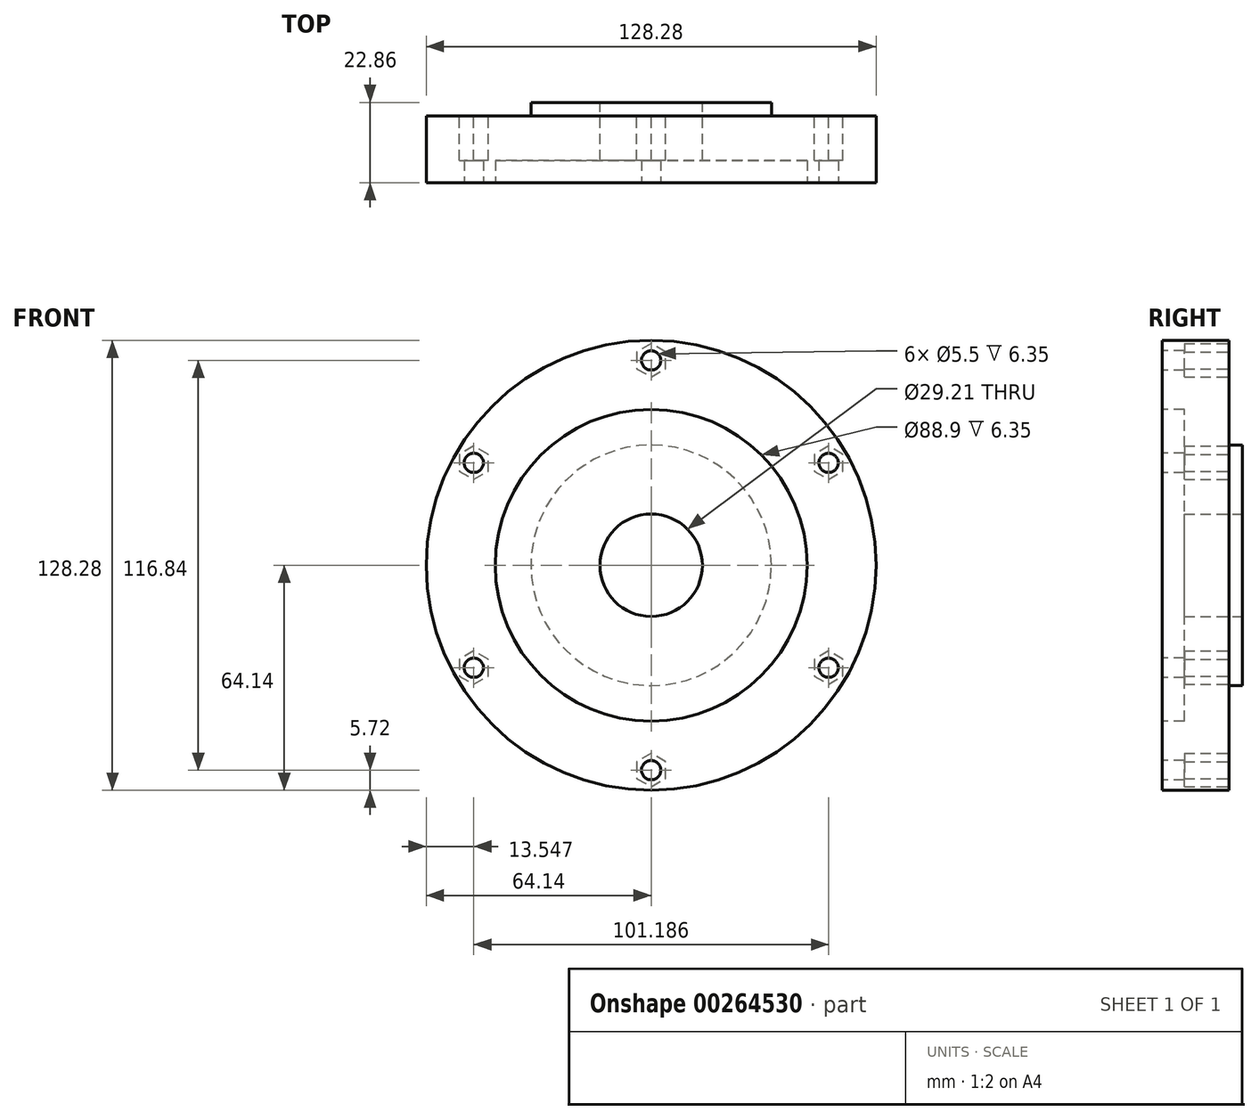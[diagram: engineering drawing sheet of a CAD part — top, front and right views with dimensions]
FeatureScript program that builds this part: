
annotation { "Feature Type Name" : "Feature", "Feature Type Description" : "" }
export const myFeature = defineFeature(function(context is Context, id is Id, definition is map)
    precondition{}
    {
        {
            var Q0;
            Q0=qCreatedBy(makeId("Front.planeOp"),FACE);
            var sketch = newSketch(context, id + "F0", { "sketchPlane" : qUnion([Q0])});
            skCircle(sketch, "E0", {"center": v(0, 0) * mm, "radius": 64.13 * mm});
            skSolve(sketch);
        }
        {
            var Q0;
            Q0 = qSketchRegion(id + "F0", true);
            extrude(context, id + "F1", {"entities" : qUnion([Q0]), "depth" : 19.05 * mm});
        }
        {
            var Q0;
            Q0=makeQuery(id+"F1.opExtrude","CAP_FACE",FACE,{"disambiguationData":[OSD([sQuery(id+"F0.wireOp",EDGE,"E0")])],"isStart":true});
            var sketch = newSketch(context, id + "F2", { "sketchPlane" : qUnion([Q0])});
            skCircle(sketch, "E1", {"center": v(0, 0) * mm, "radius": 14.6 * mm});
            skSolve(sketch);
        }
        {
            var Q0;
            Q0=makeQuery(id+"F1.opExtrude","CAP_FACE",FACE,{"disambiguationData":[OSD([sQuery(id+"F0.wireOp",EDGE,"E0")])],"isStart":true});
            var sketch = newSketch(context, id + "F3", { "sketchPlane" : qUnion([Q0])});
            skCircle(sketch, "E2", {"center": v(0, 0) * mm, "radius": 34.3 * mm});
            skSolve(sketch);
        }
        {
            var Q0;
            Q0 = qSketchRegion(id + "F3", true);
            extrude(context, id + "F4", {"entities" : qUnion([Q0]), "operationType" : NewBodyOperationType.ADD, "depth" : 3.8 * mm});
        }
        {
            var Q0;
            Q0=makeQuery(id+"F1.opExtrude","CAP_FACE",FACE,{"disambiguationData":[OSD([sQuery(id+"F0.wireOp",EDGE,"E0")])],"isStart":false});
            var sketch = newSketch(context, id + "F5", { "sketchPlane" : qUnion([Q0])});
            skCircle(sketch, "E3", {"center": v(0, 0) * mm, "radius": 12.7 * mm});
            skSolve(sketch);
        }
        {
            var Q0;
            Q0 = qSketchRegion(id + "F5", true);
            extrude(context, id + "F6", {"entities" : qUnion([Q0]), "operationType" : NewBodyOperationType.REMOVE, "endBound" : BoundingType.THROUGH_ALL, "oppositeDirection" : true, "depth" : 25.4 * mm});
        }
        {
            var Q0;
            Q0=makeQuery(id+"F1.opExtrude","CAP_FACE",FACE,{"disambiguationData":[OSD([sQuery(id+"F0.wireOp",EDGE,"E0")])],"isStart":false});
            var sketch = newSketch(context, id + "F7", { "sketchPlane" : qUnion([Q0])});
            skCircle(sketch, "E4", {"center": v(0, 0) * mm, "radius": 44.45 * mm});
            skSolve(sketch);
        }
        {
            var Q0;
            Q0 = qSketchRegion(id + "F2", true);
            extrude(context, id + "F8", {"entities" : qUnion([Q0]), "operationType" : NewBodyOperationType.REMOVE, "endBound" : BoundingType.THROUGH_ALL, "oppositeDirection" : true, "depth" : 25.4 * mm, "hasSecondDirection" : true, "secondDirectionBound" : BoundingType.THROUGH_ALL, "secondDirectionOppositeDirection" : false, "secondDirectionDepth" : 25.4 * mm});
        }
        {
            var Q0;
            Q0 = qSketchRegion(id + "F7", true);
            extrude(context, id + "F9", {"entities" : qUnion([Q0]), "operationType" : NewBodyOperationType.REMOVE, "oppositeDirection" : true, "depth" : 6.35 * mm});
        }
        {
            var Q0;
            Q0=makeQuery(id+"F9.boolean.opBoolean","COPY",FACE,{"derivedFrom":makeQuery(id+"F9.opExtrude","CAP_FACE",FACE,{"disambiguationData":[OSD([sQuery(id+"F7.wireOp",EDGE,"E4")])],"isStart":false})});
            var sketch = newSketch(context, id + "F14", { "sketchPlane" : qUnion([Q0])});
            skCircle(sketch, "E5", {"center": v(0, 0) * mm, "radius": 27.94 * mm});
            skSolve(sketch);
        }
        {
            var Q0;
            Q0=makeQuery(id+"F1.opExtrude","CAP_FACE",FACE,{"disambiguationData":[OSD([sQuery(id+"F0.wireOp",EDGE,"E0")])],"isStart":true});
            var sketch = newSketch(context, id + "F10", { "sketchPlane" : qUnion([Q0])});
            skSolve(sketch);
        }
        {
            var Q0;
            Q0=makeQuery(id+"F10.imprint","IMPRINT",FACE,{"disambiguationData":[TD([[makeQuery(id+"F10.imprint","IMPRINT",EDGE,{"derivedFrom":makeQuery(id+"F1.opExtrude","CAP_EDGE",EDGE,{"disambiguationData":[OSD([sQuery(id+"F0.wireOp",EDGE,"E0")])],"isStart":true})}),-1.0]])]});
            var sketch = newSketch(context, id + "F11", { "sketchPlane" : qUnion([Q0])});
            skCircle(sketch, "E6.cCircle", {"center": v(0, 0) * mm, "radius": 58.42 * mm, "construction": true});
            skLineSegment(sketch, "E6.0", {"start": v(50.6, 29.2) * mm, "end": v(50.6, -29.2) * mm, "construction": true});
            skLineSegment(sketch, "E6.1", {"start": v(50.6, -29.2) * mm, "end": v(0, -58.42) * mm, "construction": true});
            skLineSegment(sketch, "E6.2", {"start": v(0, -58.42) * mm, "end": v(-50.6, -29.2) * mm, "construction": true});
            skLineSegment(sketch, "E6.3", {"start": v(-50.6, -29.2) * mm, "end": v(-50.6, 29.2) * mm, "construction": true});
            skLineSegment(sketch, "E6.4", {"start": v(-50.6, 29.2) * mm, "end": v(0, 58.42) * mm, "construction": true});
            skLineSegment(sketch, "E6.5", {"start": v(0, 58.42) * mm, "end": v(50.6, 29.2) * mm, "construction": true});
            skCircle(sketch, "E7.cCircle", {"center": v(0, -58.42) * mm, "radius": 4.75 * mm, "construction": true});
            skLineSegment(sketch, "E7.0", {"start": v(4.11, -56.05) * mm, "end": v(4.11, -60.8) * mm});
            skLineSegment(sketch, "E7.1", {"start": v(4.11, -60.8) * mm, "end": v(0, -63.17) * mm});
            skLineSegment(sketch, "E7.2", {"start": v(0, -63.17) * mm, "end": v(-4.11, -60.8) * mm});
            skLineSegment(sketch, "E7.3", {"start": v(-4.11, -60.8) * mm, "end": v(-4.11, -56.04) * mm});
            skLineSegment(sketch, "E7.4", {"start": v(-4.11, -56.04) * mm, "end": v(0, -53.67) * mm});
            skLineSegment(sketch, "E7.5", {"start": v(0, -53.67) * mm, "end": v(4.11, -56.05) * mm});
            skCircle(sketch, "E8.1.0", {"center": v(50.6, -29.21) * mm, "radius": 4.75 * mm, "construction": true});
            skLineSegment(sketch, "E8.1.1", {"start": v(46.48, -31.58) * mm, "end": v(46.48, -26.83) * mm});
            skLineSegment(sketch, "E8.1.2", {"start": v(54.7, -31.59) * mm, "end": v(50.6, -33.96) * mm});
            skLineSegment(sketch, "E8.1.3", {"start": v(50.6, -33.96) * mm, "end": v(46.48, -31.58) * mm});
            skLineSegment(sketch, "E8.1.4", {"start": v(50.6, -24.46) * mm, "end": v(54.7, -26.84) * mm});
            skLineSegment(sketch, "E8.1.5", {"start": v(54.7, -26.84) * mm, "end": v(54.7, -31.59) * mm});
            skLineSegment(sketch, "E8.1.6", {"start": v(46.48, -26.83) * mm, "end": v(50.6, -24.46) * mm});
            skCircle(sketch, "E8.2.0", {"center": v(50.6, 29.2) * mm, "radius": 4.75 * mm, "construction": true});
            skLineSegment(sketch, "E8.2.1", {"start": v(50.6, 24.46) * mm, "end": v(46.48, 26.83) * mm});
            skLineSegment(sketch, "E8.2.2", {"start": v(54.7, 31.58) * mm, "end": v(54.7, 26.83) * mm});
            skLineSegment(sketch, "E8.2.3", {"start": v(54.7, 26.83) * mm, "end": v(50.6, 24.46) * mm});
            skLineSegment(sketch, "E8.2.4", {"start": v(46.48, 31.58) * mm, "end": v(50.6, 33.96) * mm});
            skLineSegment(sketch, "E8.2.5", {"start": v(50.6, 33.96) * mm, "end": v(54.7, 31.58) * mm});
            skLineSegment(sketch, "E8.2.6", {"start": v(46.48, 26.83) * mm, "end": v(46.48, 31.58) * mm});
            skCircle(sketch, "E8.3.0", {"center": v(0, 58.42) * mm, "radius": 4.75 * mm, "construction": true});
            skLineSegment(sketch, "E8.3.1", {"start": v(4.11, 56.04) * mm, "end": v(0, 53.67) * mm});
            skLineSegment(sketch, "E8.3.2", {"start": v(0, 63.17) * mm, "end": v(4.11, 60.8) * mm});
            skLineSegment(sketch, "E8.3.3", {"start": v(4.11, 60.8) * mm, "end": v(4.11, 56.04) * mm});
            skLineSegment(sketch, "E8.3.4", {"start": v(-4.11, 56.05) * mm, "end": v(-4.11, 60.8) * mm});
            skLineSegment(sketch, "E8.3.5", {"start": v(-4.11, 60.8) * mm, "end": v(0, 63.17) * mm});
            skLineSegment(sketch, "E8.3.6", {"start": v(0, 53.67) * mm, "end": v(-4.11, 56.05) * mm});
            skCircle(sketch, "E8.4.0", {"center": v(-50.6, 29.21) * mm, "radius": 4.75 * mm, "construction": true});
            skLineSegment(sketch, "E8.4.1", {"start": v(-46.48, 31.59) * mm, "end": v(-46.48, 26.83) * mm});
            skLineSegment(sketch, "E8.4.2", {"start": v(-54.7, 31.59) * mm, "end": v(-50.6, 33.96) * mm});
            skLineSegment(sketch, "E8.4.3", {"start": v(-50.6, 33.96) * mm, "end": v(-46.48, 31.58) * mm});
            skLineSegment(sketch, "E8.4.4", {"start": v(-50.6, 24.46) * mm, "end": v(-54.7, 26.84) * mm});
            skLineSegment(sketch, "E8.4.5", {"start": v(-54.7, 26.84) * mm, "end": v(-54.7, 31.59) * mm});
            skLineSegment(sketch, "E8.4.6", {"start": v(-46.48, 26.84) * mm, "end": v(-50.6, 24.46) * mm});
            skCircle(sketch, "E8.5.0", {"center": v(-50.6, -29.2) * mm, "radius": 4.75 * mm, "construction": true});
            skLineSegment(sketch, "E8.5.1", {"start": v(-50.6, -24.46) * mm, "end": v(-46.48, -26.84) * mm});
            skLineSegment(sketch, "E8.5.2", {"start": v(-54.7, -31.58) * mm, "end": v(-54.7, -26.83) * mm});
            skLineSegment(sketch, "E8.5.3", {"start": v(-54.7, -26.83) * mm, "end": v(-50.6, -24.46) * mm});
            skLineSegment(sketch, "E8.5.4", {"start": v(-46.48, -31.58) * mm, "end": v(-50.6, -33.96) * mm});
            skLineSegment(sketch, "E8.5.5", {"start": v(-50.6, -33.96) * mm, "end": v(-54.7, -31.58) * mm});
            skLineSegment(sketch, "E8.5.6", {"start": v(-46.48, -26.84) * mm, "end": v(-46.48, -31.59) * mm});
            skSolve(sketch);
        }
        {
            var Q0;
            Q0 = qSketchRegion(id + "F11", true);
            extrude(context, id + "F12", {"entities" : qUnion([Q0]), "operationType" : NewBodyOperationType.REMOVE, "oppositeDirection" : true, "depth" : 12.7 * mm});
        }
        {
            var Q0;
            Q0=sQuery(id+"F11.wireOp",VERTEX,"E8.2.0.center");
            var Q1;
            Q1=sQuery(id+"F11.wireOp",VERTEX,"E8.1.0.center");
            var Q2;
            Q2=sQuery(id+"F11.wireOp",VERTEX,"E7.cCircle.center");
            var Q3;
            Q3=sQuery(id+"F11.wireOp",VERTEX,"E6.3.start");
            var Q4;
            Q4=sQuery(id+"F11.wireOp",VERTEX,"E6.4.start");
            var Q5;
            Q5=sQuery(id+"F11.wireOp",VERTEX,"E6.5.start");
            var Q6;
            Q6=makeQuery(id+"F1.opExtrude","SWEPT_BODY",BODY,{"disambiguationData":[OSD([sQuery(id+"F0.wireOp",EDGE,"E0")])]});
            hole(context, id + "F13", {"style" : HoleStyle.SIMPLE, "endStyle" : HoleEndStyle.THROUGH, "standardTappedOrClearance" : lookupTablePath({ "standard" : "ISO", "fit" : "Normal", "size" : "M5", "type" : "Clearance" }), "standardBlindInLast" : lookupTablePath({ "fit" : "Standard", "standard" : "ISO", "size" : "M5", "type" : "Clearance" }), "holeDiameter" : 5.5 * mm, "tappedDepth" : 12.7 * mm, "tapClearance" : 3, "locations" : qUnion([Q0, Q1, Q2, Q3, Q4, Q5]), "scope" : qUnion([Q6]), "startStyle" : HoleStartStyle.PART});
        }
    });
